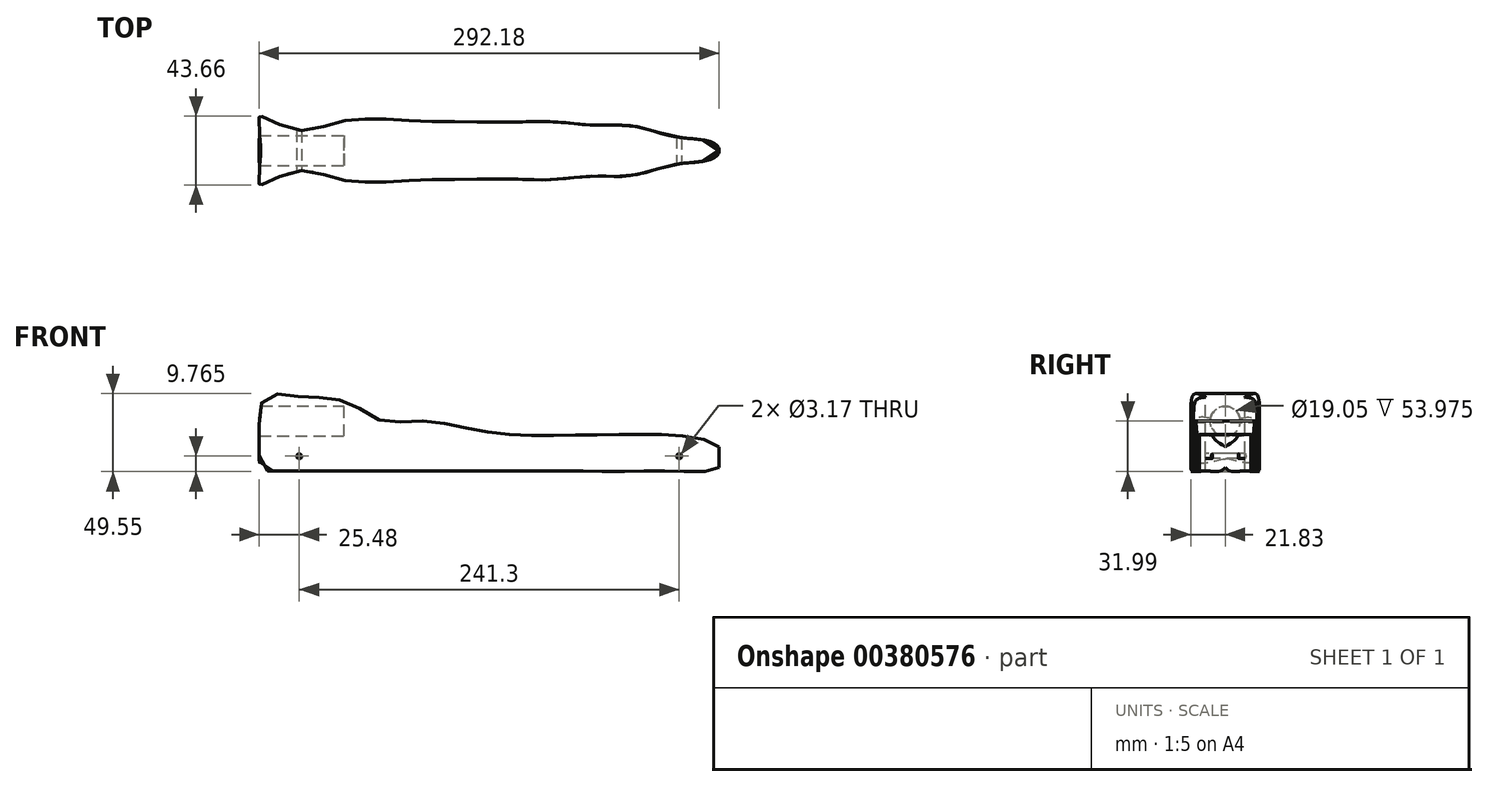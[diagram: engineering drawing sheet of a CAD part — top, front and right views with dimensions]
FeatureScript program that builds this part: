
annotation { "Feature Type Name" : "Feature", "Feature Type Description" : "" }
export const myFeature = defineFeature(function(context is Context, id is Id, definition is map)
    precondition{}
    {
        {
            var Q0;
            Q0=qCreatedBy(makeId("Front.planeOp"),FACE);
            var sketch = newSketch(context, id + "F0", { "sketchPlane" : qUnion([Q0])});
            skLineSegment(sketch, "E0.bottom", {"start": v(-146.05, 31.75) * mm, "end": v(146.05, 31.75) * mm, "construction": true});
            skLineSegment(sketch, "E0.top", {"start": v(-146.05, -31.75) * mm, "end": v(146.05, -31.75) * mm, "construction": true});
            skLineSegment(sketch, "E0.right", {"start": v(146.05, 31.75) * mm, "end": v(146.05, -31.75) * mm, "construction": true});
            skFitSpline(sketch, "E1", {"points": [v(-146.05, -24.02) * mm, v(-146.05, 0) * mm, v(-141.8, 16.4) * mm, v(-128.08, 16.4) * mm, v(-105.79, 14.94) * mm, v(-95.25, 13.47) * mm, v(-85.86, 10.18) * mm, v(-67.32, 0) * mm, v(-52.87, 0) * mm, v(-46.5, 0) * mm, v(-38.17, 0) * mm, v(0, -7.04) * mm, v(33.42, -8.95) * mm, v(87.5, -8.49) * mm, v(127.36, -9.86) * mm, v(144.9, -14.14) * mm, v(146.05, -16.33) * mm, v(146.05, -29.22) * mm, v(145.59, -31.27) * mm, v(144.47, -31.75) * mm, v(115.4, -31.75) * mm, v(90.89, -31.75) * mm, v(68.29, -31.75) * mm, v(46.65, -31.75) * mm, v(19.14, -31.75) * mm, v(-6.96, -31.75) * mm, v(-28.04, -31.75) * mm, v(-58.88, -31.75) * mm, v(-90.58, -31.75) * mm, v(-95.25, -31.75) * mm, v(-137.5, -31.75) * mm, v(-144.78, -30.62) * mm, v(-146.05, -24.02) * mm]});
            skLineSegment(sketch, "E2.bottom", {"start": v(-146.05, 9.52) * mm, "end": v(-95.25, 9.52) * mm, "construction": true});
            skLineSegment(sketch, "E2.top", {"start": v(-141.83, -9.52) * mm, "end": v(-95.25, -9.52) * mm, "construction": true});
            skLineSegment(sketch, "E2.right", {"start": v(-95.25, 9.52) * mm, "end": v(-95.25, -9.52) * mm, "construction": true});
            skLineSegment(sketch, "E3", {"start": v(-146.05, 31.75) * mm, "end": v(-146.05, -31.75) * mm, "construction": true});
            skSolve(sketch);
        }
        {
            var Q0;
            Q0=qCreatedBy(makeId("Top.planeOp"),FACE);
            var sketch = newSketch(context, id + "F1", { "sketchPlane" : qUnion([Q0])});
            skLineSegment(sketch, "E4.bottom", {"start": v(-146.05, 22.22) * mm, "end": v(146.05, 22.23) * mm, "construction": true});
            skLineSegment(sketch, "E4.top", {"start": v(-146.05, -22.23) * mm, "end": v(146.05, -22.22) * mm, "construction": true});
            skLineSegment(sketch, "E4.left", {"start": v(-146.05, 22.22) * mm, "end": v(-146.05, -22.23) * mm, "construction": true});
            skLineSegment(sketch, "E4.right", {"start": v(146.05, 22.22) * mm, "end": v(146.05, -22.22) * mm, "construction": true});
            skLineSegment(sketch, "E5", {"start": v(-146.05, 0) * mm, "end": v(146.05, 0) * mm, "construction": true});
            skFitSpline(sketch, "E6", {"points": [v(-146.05, 0) * mm, v(-146.04, 20) * mm, v(-145.68, 21.83) * mm, v(-121.57, 12.87) * mm, v(-94.24, 18.62) * mm, v(-44.82, 18.71) * mm, v(-25.76, 18.49) * mm, v(11.44, 18.03) * mm, v(38.54, 18.49) * mm, v(56.9, 16.88) * mm, v(71.6, 16.19) * mm, v(86.76, 16.19) * mm, v(102.5, 12.98) * mm, v(122.7, 8.17) * mm, v(146.05, 0) * mm], "startDerivative": vector(0, 335.54) * mm, "endDerivative": vector(0, -277.49) * mm});
            skFitSpline(sketch, "E7.MirrorCS", {"points": [v(-146.05, 0) * mm, v(-146.04, -20) * mm, v(-145.68, -21.83) * mm, v(-121.57, -12.87) * mm, v(-94.24, -18.62) * mm, v(-44.82, -18.71) * mm, v(-25.76, -18.49) * mm, v(11.44, -18.03) * mm, v(38.54, -18.49) * mm, v(56.9, -16.88) * mm, v(71.6, -16.19) * mm, v(86.76, -16.19) * mm, v(102.5, -12.98) * mm, v(122.7, -8.17) * mm, v(146.05, 0) * mm], "startDerivative": vector(0, -335.54) * mm, "endDerivative": vector(0, 277.49) * mm});
            skLineSegment(sketch, "E8.MirrorCS", {"start": v(-146.05, -22.23) * mm, "end": v(146.05, -22.23) * mm});
            skPoint(sketch, "E9", {"position": v(0, 22.22) * mm});
            skSolve(sketch);
        }
        {
            var Q0;
            Q0=qCreatedBy(makeId("Right.planeOp"),FACE);
            var sketch = newSketch(context, id + "F2", { "sketchPlane" : qUnion([Q0])});
            skCircle(sketch, "E10", {"center": v(0, 0) * mm, "radius": 9.53 * mm});
            skSolve(sketch);
        }
        {
            var Q0;
            Q0=qCreatedBy(makeId("Front.planeOp"),FACE);
            var sketch = newSketch(context, id + "F3", { "sketchPlane" : qUnion([Q0])});
            skCircle(sketch, "E11", {"center": v(-120.65, -22.22) * mm, "radius": 1.59 * mm});
            skCircle(sketch, "E12", {"center": v(120.65, -22.23) * mm, "radius": 1.59 * mm});
            skSolve(sketch);
        }
        {
            var Q0;
            Q0=qSketchRegion(id+"F0",true);
            extrude(context, id + "F4", {"entities" : qUnion([Q0]), "depth" : 44.45 * mm, "symmetric" : true});
        }
        {
            var Q0;
            Q0=qSketchRegion(id+"F1",true);
            extrude(context, id + "F5", {"entities" : qUnion([Q0]), "operationType" : NewBodyOperationType.INTERSECT, "endBound" : BoundingType.THROUGH_ALL, "oppositeDirection" : true, "depth" : 60.96 * mm, "hasSecondDirection" : true, "secondDirectionBound" : BoundingType.THROUGH_ALL, "secondDirectionOppositeDirection" : false, "secondDirectionDepth" : 25.4 * mm});
        }
        {
            var Q0;
            Q0=qSketchRegion(id+"F2",true);
            extrude(context, id + "F6", {"entities" : qUnion([Q0]), "operationType" : NewBodyOperationType.REMOVE, "oppositeDirection" : true, "depth" : 152.4 * mm, "hasSecondDirection" : true, "secondDirectionOppositeDirection" : true, "secondDirectionDepth" : 92.07 * mm});
        }
        {
            var Q0;
            Q0=qSketchRegion(id+"F3",true);
            extrude(context, id + "F7", {"entities" : qUnion([Q0]), "operationType" : NewBodyOperationType.REMOVE, "oppositeDirection" : true, "depth" : 50.8 * mm, "symmetric" : true});
        }
    });
